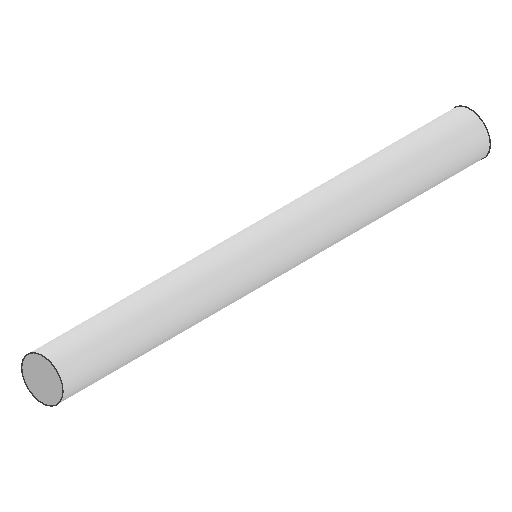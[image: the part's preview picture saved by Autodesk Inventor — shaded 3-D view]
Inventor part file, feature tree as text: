
AUTODESK INVENTOR PART (.ipt)
format: ipt  version: 2025.2 (Build 292293000, 293)  size: 84,992 bytes
history: native  units: in
note: dims shown in document units (in); Inventor stores cm internally (conversion verified against a paired STEP export)
features: extrude x1, sketch x1
ambient origin geometry x8: Origin, YZ Plane, XZ Plane, XY Plane, X Axis, Y Axis, Z Axis, Center Point
bodies: Solid1 (feature_tree)
feature tree (2):
  extrude  "Extrusion1"  Depth=3.25in TaperAngle=0.0deg
  sketch  "Sketch1"  dims[d0=0.315in d1=3.25in d2=0.0in]
